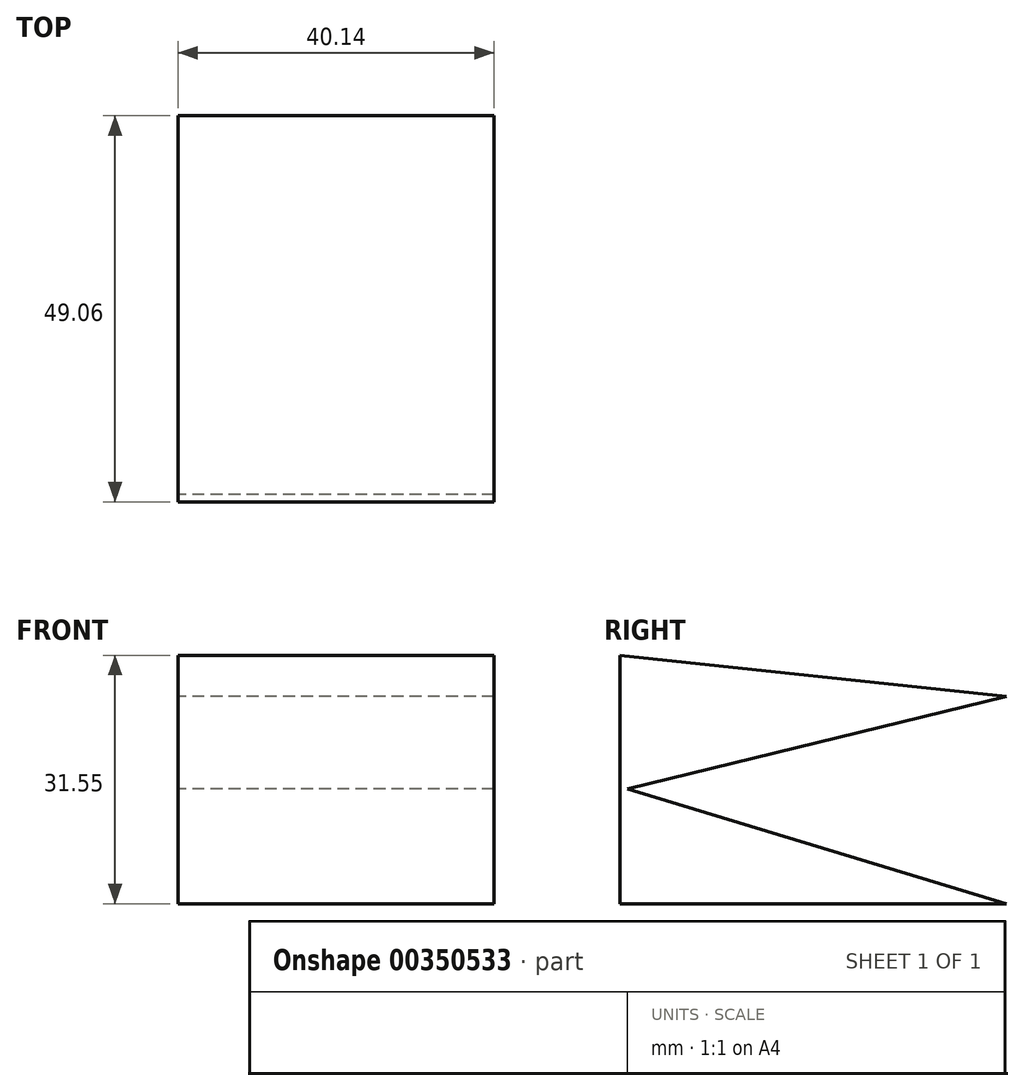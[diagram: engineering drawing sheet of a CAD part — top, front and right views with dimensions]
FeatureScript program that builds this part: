
annotation { "Feature Type Name" : "Feature", "Feature Type Description" : "" }
export const myFeature = defineFeature(function(context is Context, id is Id, definition is map)
    precondition{}
    {
        {
            var Q0;
            Q0=qCreatedBy(makeId("Right.planeOp"),FACE);
            var sketch = newSketch(context, id + "F0", { "sketchPlane" : qUnion([Q0])});
            skLineSegment(sketch, "E0", {"start": v(0, 0) * mm, "end": v(-49.06, 0) * mm});
            skLineSegment(sketch, "E1", {"start": v(-48.12, 14.58) * mm, "end": v(0, 0) * mm});
            skLineSegment(sketch, "E2", {"start": v(0, 0) * mm, "end": v(0, 26.32) * mm});
            skLineSegment(sketch, "E3", {"start": v(0, 26.32) * mm, "end": v(-49.06, 31.55) * mm});
            skLineSegment(sketch, "E4", {"start": v(-48.12, 14.58) * mm, "end": v(0, 26.32) * mm});
            skLineSegment(sketch, "E5", {"start": v(-49.06, 0) * mm, "end": v(-49.06, 31.55) * mm});
            skSolve(sketch);
        }
        {
            var Q0;
            Q0=makeQuery(id+"F0.imprint","IMPRINT",FACE,{"disambiguationData":[TD([[makeQuery(id+"F0.imprint","IMPRINT",EDGE,{"derivedFrom":sQuery(id+"F0.wireOp",EDGE,"E0")}),-1.0]])]});
            extrude(context, id + "F1", {"entities" : qUnion([Q0]), "endBound" : BoundingType.SYMMETRIC, "depth" : 40.13 * mm});
        }
    });
